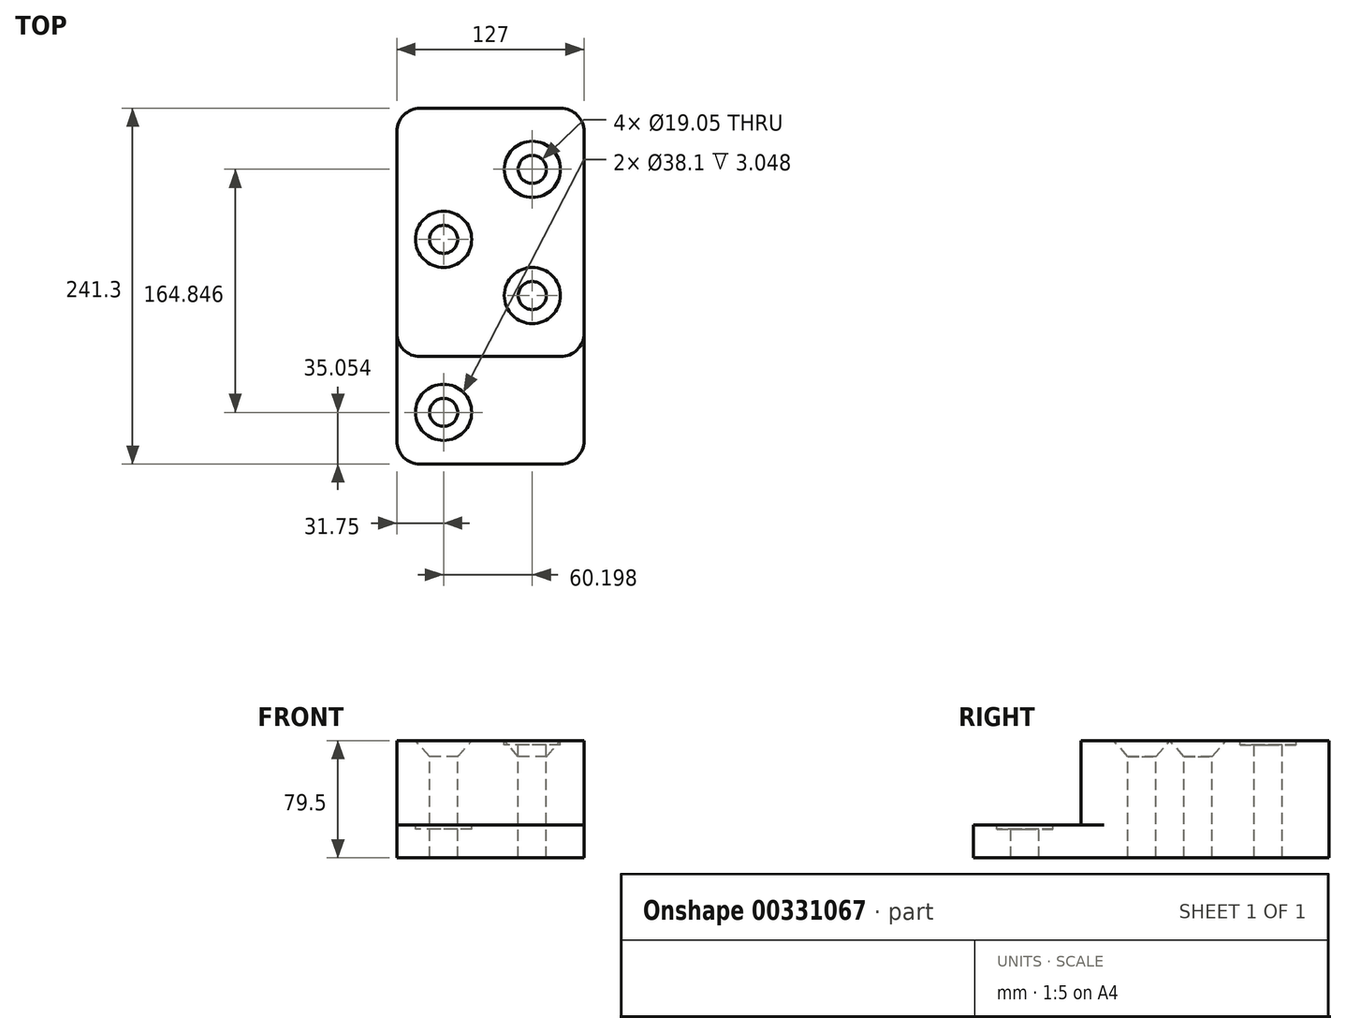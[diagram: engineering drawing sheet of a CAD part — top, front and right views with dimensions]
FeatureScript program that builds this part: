
annotation { "Feature Type Name" : "Feature", "Feature Type Description" : "" }
export const myFeature = defineFeature(function(context is Context, id is Id, definition is map)
    precondition{}
    {
        {
            var Q0;
            Q0=qCreatedBy(makeId("Top.planeOp"),FACE);
            var sketch = newSketch(context, id + "F0", { "sketchPlane" : qUnion([Q0])});
            skLineSegment(sketch, "E0.bottom", {"start": v(0, 0) * mm, "end": v(127, 0) * mm});
            skLineSegment(sketch, "E0.top", {"start": v(0, 168.4) * mm, "end": v(127, 168.4) * mm});
            skLineSegment(sketch, "E0.left", {"start": v(0, 0) * mm, "end": v(0, 168.4) * mm});
            skLineSegment(sketch, "E0.right", {"start": v(127, 0) * mm, "end": v(127, 168.4) * mm});
            skSolve(sketch);
        }
        {
            var Q0;
            Q0 = qSketchRegion(id + "F0", true);
            extrude(context, id + "F1", {"entities" : qUnion([Q0]), "depth" : 79.5 * mm});
        }
        {
            var Q0;
            Q0=qCreatedBy(makeId("Top.planeOp"),FACE);
            var sketch = newSketch(context, id + "F2", { "sketchPlane" : qUnion([Q0])});
            skLineSegment(sketch, "E1.bottom", {"start": v(0, 0) * mm, "end": v(127, 0) * mm});
            skLineSegment(sketch, "E1.top", {"start": v(0, -72.9) * mm, "end": v(127, -72.9) * mm});
            skLineSegment(sketch, "E1.left", {"start": v(0, 0) * mm, "end": v(0, -72.9) * mm});
            skLineSegment(sketch, "E1.right", {"start": v(127, 0) * mm, "end": v(127, -72.9) * mm});
            skLineSegment(sketch, "E2.0", {"start": v(127, 0) * mm, "end": v(127, 168.4) * mm});
            skSolve(sketch);
        }
        {
            var Q0;
            Q0=makeQuery(id+"F2.imprint","IMPRINT",FACE,{"disambiguationData":[TD([[makeQuery(id+"F2.imprint","IMPRINT",EDGE,{"derivedFrom":sQuery(id+"F2.wireOp",EDGE,"E1.bottom")}),-1.0]])]});
            extrude(context, id + "F3", {"entities" : qUnion([Q0]), "operationType" : NewBodyOperationType.ADD, "depth" : 22.35 * mm});
        }
        {
            var Q0;
            Q0=makeQuery(id+"F1.opExtrude","SWEPT_EDGE",EDGE,{"disambiguationData":[OSD([sQuery(id+"F0.wireOp",EDGE,"E0.bottom"),sQuery(id+"F0.wireOp",EDGE,"E0.right")])]});
            var Q1;
            Q1=makeQuery(id+"F3.opExtrude","SWEPT_EDGE",EDGE,{"disambiguationData":[OSD([sQuery(id+"F2.wireOp",EDGE,"E1.top"),sQuery(id+"F2.wireOp",EDGE,"E1.right")])]});
            var Q2;
            Q2=makeQuery(id+"F3.opExtrude","SWEPT_EDGE",EDGE,{"disambiguationData":[OSD([sQuery(id+"F2.wireOp",EDGE,"E1.top"),sQuery(id+"F2.wireOp",EDGE,"E1.left")])]});
            var Q3;
            Q3=makeQuery(id+"F1.opExtrude","SWEPT_EDGE",EDGE,{"disambiguationData":[OSD([sQuery(id+"F0.wireOp",EDGE,"E0.bottom"),sQuery(id+"F0.wireOp",EDGE,"E0.left")])]});
            var Q4;
            Q4=makeQuery(id+"F1.opExtrude","SWEPT_EDGE",EDGE,{"disambiguationData":[OSD([sQuery(id+"F0.wireOp",EDGE,"E0.top"),sQuery(id+"F0.wireOp",EDGE,"E0.right")])]});
            var Q5;
            Q5=makeQuery(id+"F1.opExtrude","SWEPT_EDGE",EDGE,{"disambiguationData":[OSD([sQuery(id+"F0.wireOp",EDGE,"E0.top"),sQuery(id+"F0.wireOp",EDGE,"E0.left")])]});
            fillet(context, id + "F4", {"entities" : qUnion([Q0, Q1, Q2, Q3, Q4, Q5]), "radius" : 15.75 * mm, "tangentPropagation" : true, "allowEdgeOverflow" : false});
        }
        {
            var Q0;
            Q0=makeQuery(id+"F1.opExtrude","CAP_FACE",FACE,{"disambiguationData":[OSD([sQuery(id+"F0.wireOp",EDGE,"E0.bottom"),sQuery(id+"F0.wireOp",EDGE,"E0.top"),sQuery(id+"F0.wireOp",EDGE,"E0.left"),sQuery(id+"F0.wireOp",EDGE,"E0.right")])],"isStart":false});
            var sketch = newSketch(context, id + "F5", { "sketchPlane" : qUnion([Q0])});
            skPoint(sketch, "E3", {"position": v(91.95, 127) * mm});
            skPoint(sketch, "E4", {"position": v(91.95, 41.4) * mm});
            skPoint(sketch, "E5", {"position": v(31.75, 79.5) * mm});
            skSolve(sketch);
        }
        {
            var Q0;
            Q0=sQuery(id+"F5.wireOp",VERTEX,"E5");
            var Q1;
            Q1=sQuery(id+"F5.wireOp",VERTEX,"E4");
            var Q2;
            Q2=makeQuery(id+"F1.opExtrude","SWEPT_BODY",BODY,{"disambiguationData":[OSD([sQuery(id+"F0.wireOp",EDGE,"E0.bottom"),sQuery(id+"F0.wireOp",EDGE,"E0.top"),sQuery(id+"F0.wireOp",EDGE,"E0.left"),sQuery(id+"F0.wireOp",EDGE,"E0.right")])]});
            hole(context, id + "F6", {"style" : HoleStyle.C_SINK, "endStyle" : HoleEndStyle.THROUGH, "holeDiameter" : 19.05 * mm, "cSinkDiameter" : 38.1 * mm, "cSinkAngle" : 82 * degree, "tappedDepth" : 12.7 * mm, "tapClearance" : 3, "locations" : qUnion([Q0, Q1]), "scope" : qUnion([Q2])});
        }
        {
            var Q0;
            Q0=sQuery(id+"F5.wireOp",VERTEX,"E3");
            var Q1;
            Q1=makeQuery(id+"F1.opExtrude","SWEPT_BODY",BODY,{"disambiguationData":[OSD([sQuery(id+"F0.wireOp",EDGE,"E0.bottom"),sQuery(id+"F0.wireOp",EDGE,"E0.top"),sQuery(id+"F0.wireOp",EDGE,"E0.left"),sQuery(id+"F0.wireOp",EDGE,"E0.right")])]});
            hole(context, id + "F7", {"style" : HoleStyle.C_BORE, "endStyle" : HoleEndStyle.THROUGH, "holeDiameter" : 19.05 * mm, "cBoreDiameter" : 38.1 * mm, "cBoreDepth" : 3.05 * mm, "tappedDepth" : 12.7 * mm, "tapClearance" : 3, "locations" : qUnion([Q0]), "scope" : qUnion([Q1])});
        }
        {
            var Q0;
            Q0=makeQuery(id+"F3.opExtrude","CAP_FACE",FACE,{"disambiguationData":[OSD([sQuery(id+"F2.wireOp",EDGE,"E1.bottom"),sQuery(id+"F2.wireOp",EDGE,"E1.top"),sQuery(id+"F2.wireOp",EDGE,"E1.left"),sQuery(id+"F2.wireOp",EDGE,"E1.right")])],"isStart":false});
            var sketch = newSketch(context, id + "F8", { "sketchPlane" : qUnion([Q0])});
            skPoint(sketch, "E6", {"position": v(31.75, -37.85) * mm});
            skSolve(sketch);
        }
        {
            var Q0;
            Q0=sQuery(id+"F8.wireOp",VERTEX,"E6");
            var Q1;
            Q1=makeQuery(id+"F1.opExtrude","SWEPT_BODY",BODY,{"disambiguationData":[OSD([sQuery(id+"F0.wireOp",EDGE,"E0.bottom"),sQuery(id+"F0.wireOp",EDGE,"E0.top"),sQuery(id+"F0.wireOp",EDGE,"E0.left"),sQuery(id+"F0.wireOp",EDGE,"E0.right")])]});
            hole(context, id + "F9", {"style" : HoleStyle.C_BORE, "endStyle" : HoleEndStyle.THROUGH, "holeDiameter" : 19.05 * mm, "cBoreDiameter" : 38.1 * mm, "cBoreDepth" : 3.05 * mm, "tappedDepth" : 12.7 * mm, "tapClearance" : 3, "locations" : qUnion([Q0]), "scope" : qUnion([Q1])});
        }
    });
